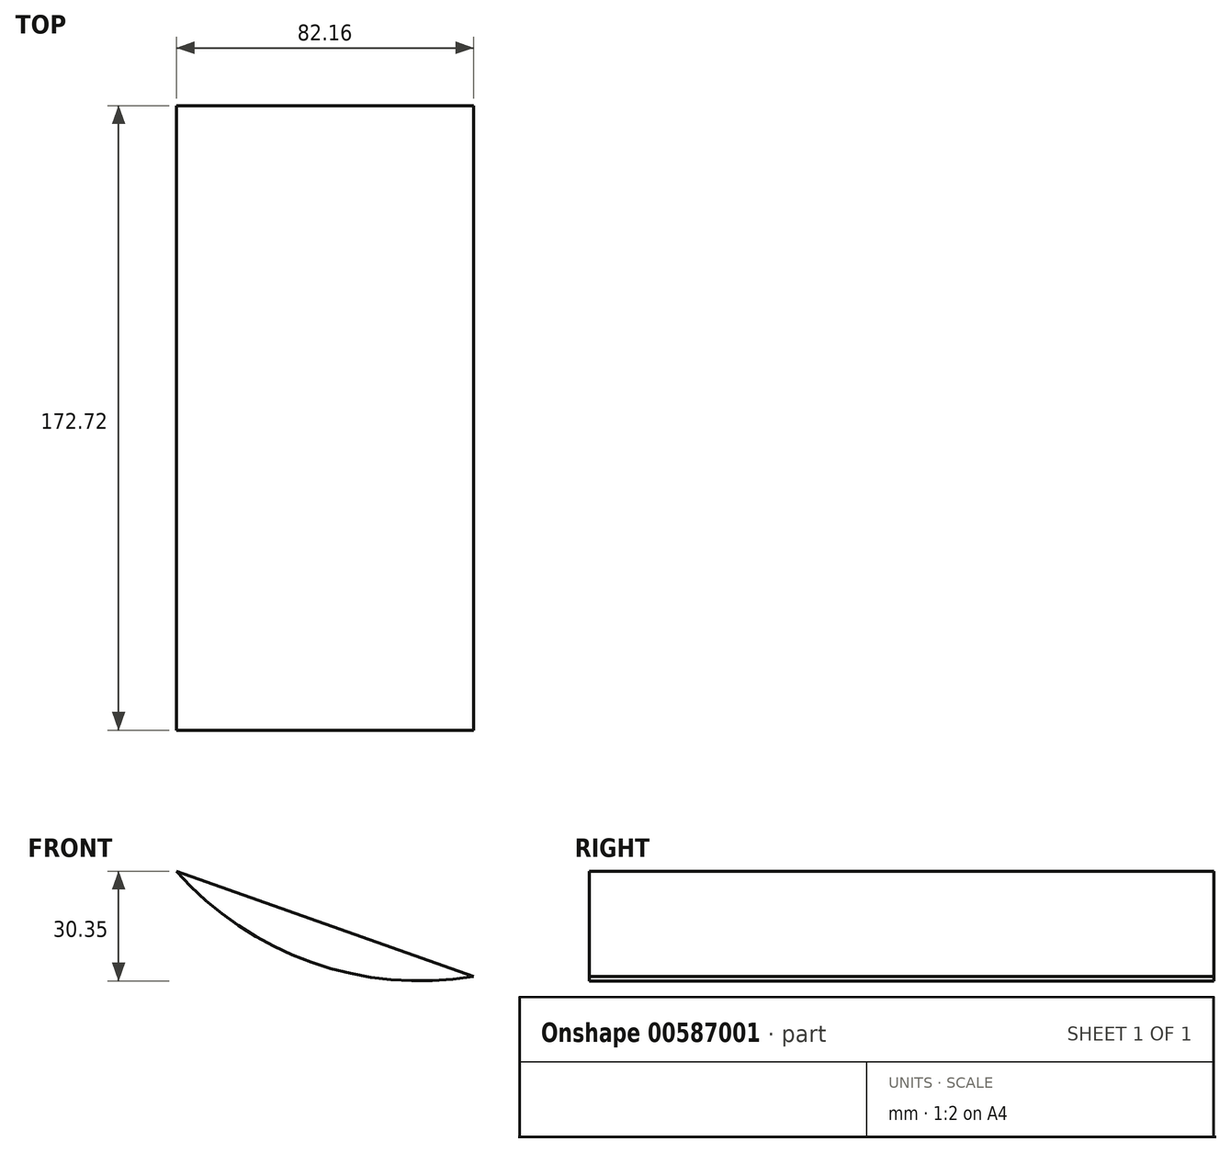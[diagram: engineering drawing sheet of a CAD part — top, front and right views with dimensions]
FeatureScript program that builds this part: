
annotation { "Feature Type Name" : "Feature", "Feature Type Description" : "" }
export const myFeature = defineFeature(function(context is Context, id is Id, definition is map)
    precondition{}
    {
        {
            var Q0;
            Q0=qCreatedBy(makeId("Front.planeOp"),FACE);
            var sketch = newSketch(context, id + "F0", { "sketchPlane" : qUnion([Q0])});
            skLineSegment(sketch, "E0", {"start": v(-119.18, 19.54) * mm, "end": v(-37.02, -9.56) * mm});
            skArc(sketch, "E1", {"start": v(-119.18, 19.54) * mm, "mid": v(-81.88, -5.67) * mm, "end": v(-37.02, -9.56) * mm});
            skSolve(sketch);
        }
        {
            var Q0;
            Q0=sQuery(id+"F0.wireOp",EDGE,"E1");
            var Q1;
            Q1=sQuery(id+"F0.wireOp",EDGE,"E0");
            extrude(context, id + "F1", {"bodyType" : ToolBodyType.SURFACE, "surfaceEntities" : qUnion([Q0, Q1]), "depth" : 172.72 * mm, "offsetDistance" : 25.4 * mm});
        }
    });
